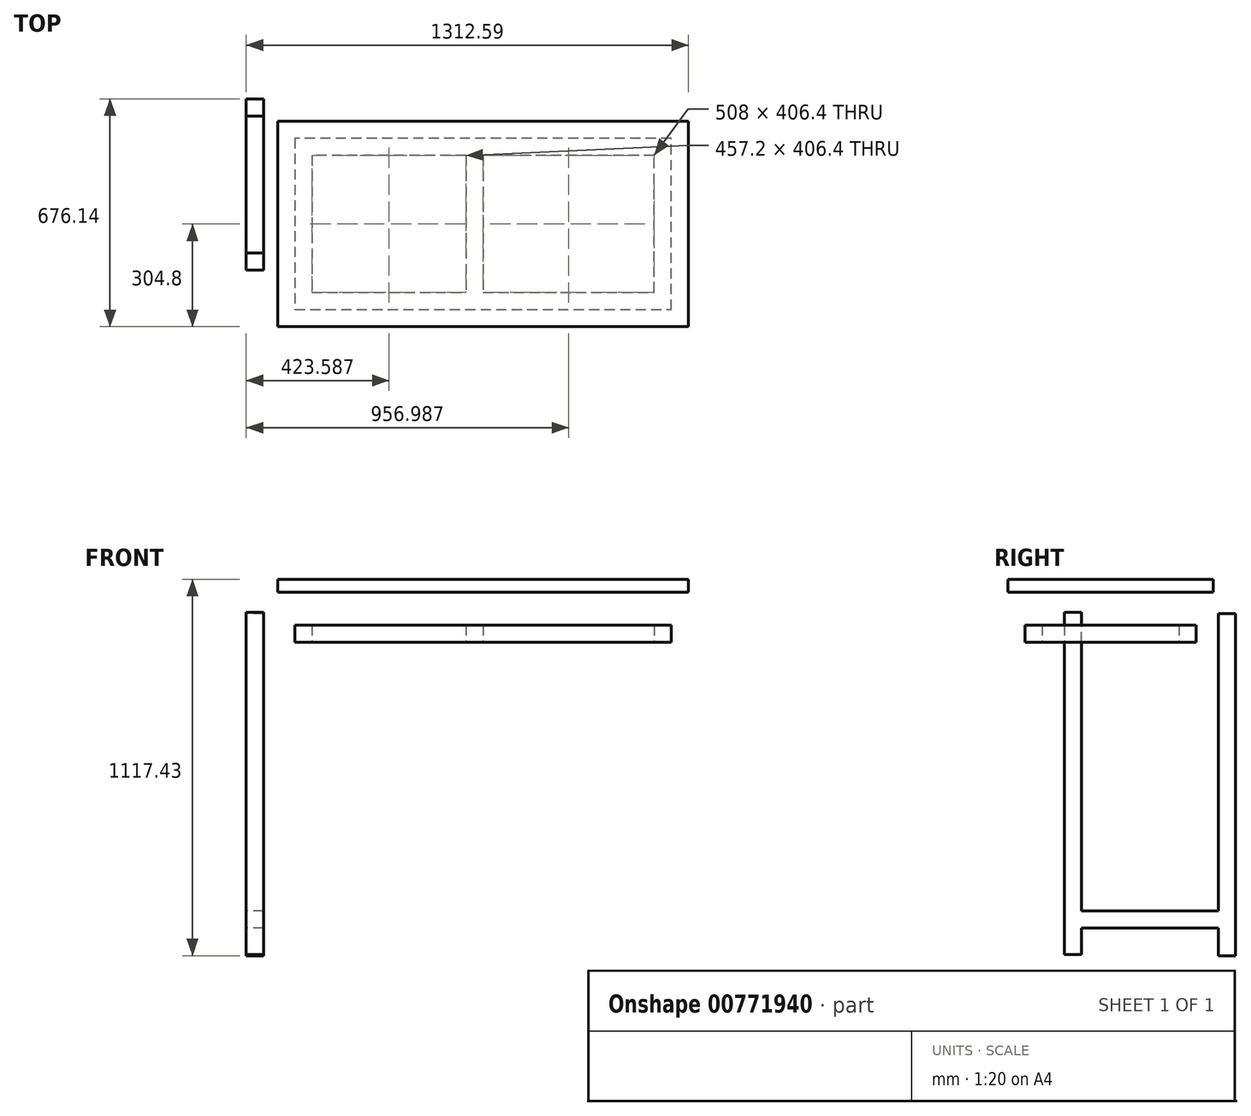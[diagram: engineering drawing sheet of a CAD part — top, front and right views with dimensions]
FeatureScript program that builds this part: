
annotation { "Feature Type Name" : "Feature", "Feature Type Description" : "" }
export const myFeature = defineFeature(function(context is Context, id is Id, definition is map)
    precondition{}
    {
        {
            var Q0;
            Q0=qCreatedBy(makeId("Right.planeOp"),FACE);
            var sketch = newSketch(context, id + "F0", { "sketchPlane" : qUnion([Q0])});
            skLineSegment(sketch, "E0", {"start": v(66.54, 85.67) * mm, "end": v(15.74, 85.67) * mm});
            skLineSegment(sketch, "E1", {"start": v(66.54, -930.33) * mm, "end": v(15.74, -930.33) * mm});
            skLineSegment(sketch, "E2", {"start": v(15.74, -930.33) * mm, "end": v(15.74, 85.67) * mm});
            skLineSegment(sketch, "E3", {"start": v(66.54, -930.33) * mm, "end": v(66.54, 85.67) * mm});
            skLineSegment(sketch, "E4", {"start": v(15.74, -797.87) * mm, "end": v(15.74, -848.67) * mm});
            skLineSegment(sketch, "E5", {"start": v(-390.66, -926.73) * mm, "end": v(-390.66, 89.27) * mm});
            skLineSegment(sketch, "E6", {"start": v(-441.46, 89.27) * mm, "end": v(-390.66, 89.27) * mm});
            skLineSegment(sketch, "E7", {"start": v(-441.46, 89.27) * mm, "end": v(-441.46, -926.73) * mm});
            skLineSegment(sketch, "E8", {"start": v(-441.46, -926.73) * mm, "end": v(-390.66, -926.73) * mm});
            skLineSegment(sketch, "E9", {"start": v(-390.66, -848.67) * mm, "end": v(15.74, -848.67) * mm});
            skLineSegment(sketch, "E10", {"start": v(15.74, -797.87) * mm, "end": v(-390.66, -797.87) * mm});
            skSolve(sketch);
        }
        {
            var Q0;
            Q0 = qSketchRegion(id + "F0", true);
            extrude(context, id + "F1", {"entities" : qUnion([Q0]), "depth" : 50.8 * mm, "offsetDistance" : 25.4 * mm});
        }
        {
            var Q0;
            Q0=qCreatedBy(makeId("Front.planeOp"),FACE);
            var sketch = newSketch(context, id + "F2", { "sketchPlane" : qUnion([Q0])});
            skLineSegment(sketch, "E11.bottom", {"start": v(93.39, 187.1) * mm, "end": v(1312.59, 187.1) * mm});
            skLineSegment(sketch, "E11.top", {"start": v(93.39, 149) * mm, "end": v(1312.59, 149) * mm});
            skLineSegment(sketch, "E11.left", {"start": v(93.39, 187.1) * mm, "end": v(93.39, 149) * mm});
            skLineSegment(sketch, "E11.right", {"start": v(1312.59, 187.1) * mm, "end": v(1312.59, 149) * mm});
            skSolve(sketch);
        }
        {
            var Q0;
            Q0 = qSketchRegion(id + "F2", true);
            extrude(context, id + "F3", {"entities" : qUnion([Q0]), "depth" : 609.6 * mm, "offsetDistance" : 25.4 * mm});
        }
        {
            var Q0;
            Q0=qCreatedBy(makeId("Top.planeOp"),FACE);
            var sketch = newSketch(context, id + "F4", { "sketchPlane" : qUnion([Q0])});
            skLineSegment(sketch, "E12.0", {"start": v(1261.79, -50.8) * mm, "end": v(144.19, -50.8) * mm});
            skLineSegment(sketch, "E12.1", {"start": v(1261.79, -558.8) * mm, "end": v(1261.79, -50.8) * mm});
            skLineSegment(sketch, "E12.2", {"start": v(144.19, -558.8) * mm, "end": v(1261.79, -558.8) * mm});
            skLineSegment(sketch, "E12.3", {"start": v(144.19, -50.8) * mm, "end": v(144.19, -558.8) * mm});
            skLineSegment(sketch, "E13.0", {"start": v(1261.79, -101.6) * mm, "end": v(144.19, -101.6) * mm});
            skLineSegment(sketch, "E14.0", {"start": v(194.99, -50.8) * mm, "end": v(194.99, -558.8) * mm});
            skLineSegment(sketch, "E15.0", {"start": v(144.19, -508) * mm, "end": v(1261.79, -508) * mm});
            skLineSegment(sketch, "E16.0", {"start": v(1210.99, -558.8) * mm, "end": v(1210.99, -50.8) * mm});
            skLineSegment(sketch, "E17.0", {"start": v(652.19, -50.8) * mm, "end": v(652.19, -558.8) * mm});
            skLineSegment(sketch, "E18.0", {"start": v(702.99, -50.8) * mm, "end": v(702.99, -558.8) * mm});
            skSolve(sketch);
        }
        {
            var Q0;
            Q0 = qSketchRegion(id + "F4", true);
            var Q1;
            {var subQ0=sQuery(id+"F4.wireOp",EDGE,"E18.0");var subQ1=sQuery(id+"F4.wireOp",EDGE,"E13.0");var subQ2=makeQuery(id+"F4.imprint","INTERSECT",VERTEX,{"derivedFrom":[subQ1,subQ0]});Q1=makeQuery(id+"F4.imprint","IMPRINT",FACE,{"disambiguationData":[TD([[makeQuery(id+"F4.imprint","IMPRINT",EDGE,{"disambiguationData":[TD([[subQ2,-1.0]])],"derivedFrom":subQ1}),1.0]])]});}
            extrude(context, id + "F5", {"entities" : qUnion([Q0, Q1]), "depth" : 50.8 * mm, "offsetDistance" : 25.4 * mm});
        }
    });
